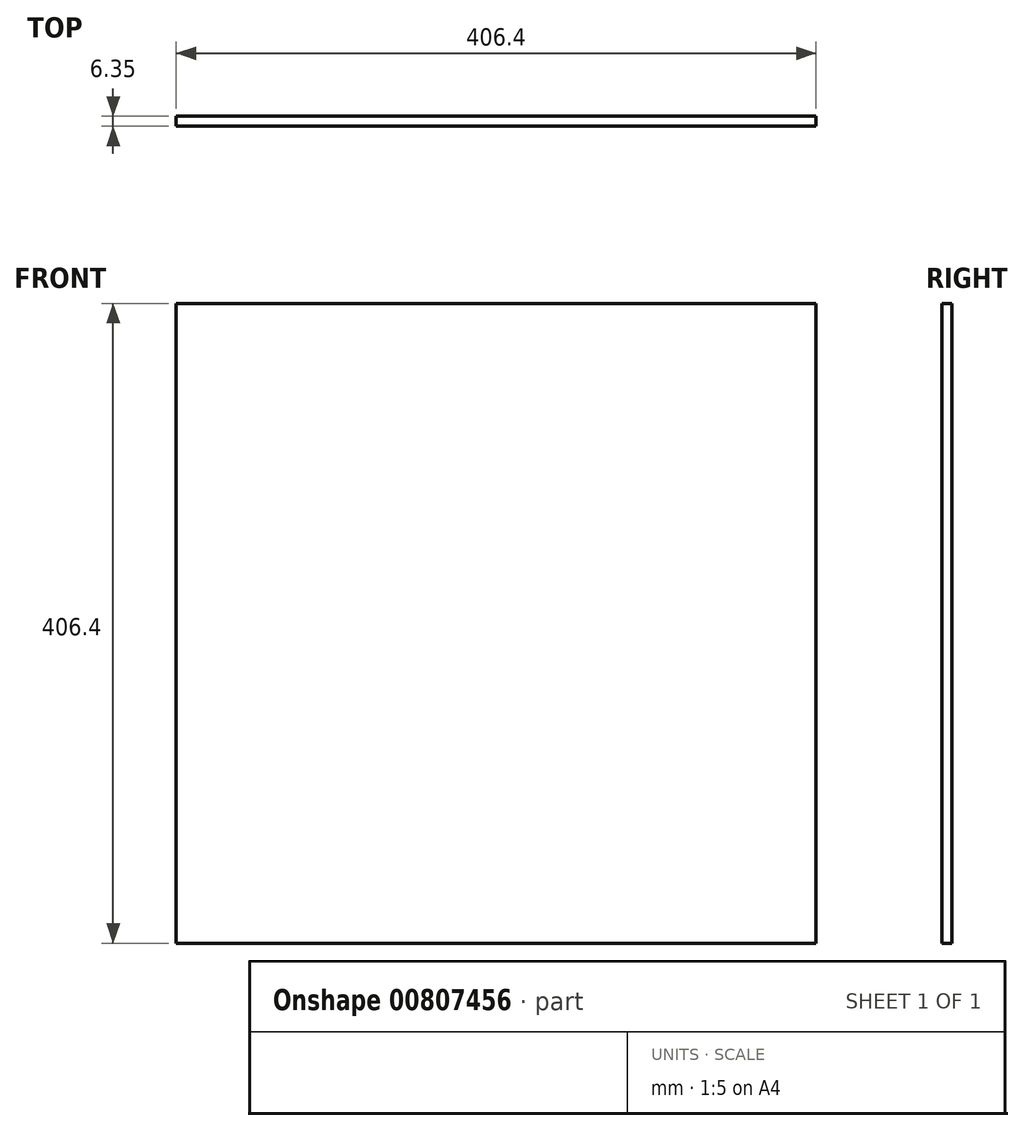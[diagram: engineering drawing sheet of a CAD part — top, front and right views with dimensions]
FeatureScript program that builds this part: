
annotation { "Feature Type Name" : "Feature", "Feature Type Description" : "" }
export const myFeature = defineFeature(function(context is Context, id is Id, definition is map)
    precondition{}
    {
        {
            var Q0;
            Q0=qCreatedBy(makeId("Front.planeOp"),FACE);
            var sketch = newSketch(context, id + "F0", { "sketchPlane" : qUnion([Q0])});
            skLineSegment(sketch, "E0.bottom", {"start": v(0, 0) * mm, "end": v(406.4, 0) * mm});
            skLineSegment(sketch, "E0.top", {"start": v(0, 406.4) * mm, "end": v(406.4, 406.4) * mm});
            skLineSegment(sketch, "E0.left", {"start": v(0, 0) * mm, "end": v(0, 406.4) * mm});
            skLineSegment(sketch, "E0.right", {"start": v(406.4, 0) * mm, "end": v(406.4, 406.4) * mm});
            skSolve(sketch);
        }
        {
            var Q0;
            Q0 = qSketchRegion(id + "F0", true);
            extrude(context, id + "F1", {"entities" : qUnion([Q0]), "depth" : 6.35 * mm, "offsetDistance" : 25.4 * mm});
        }
    });
